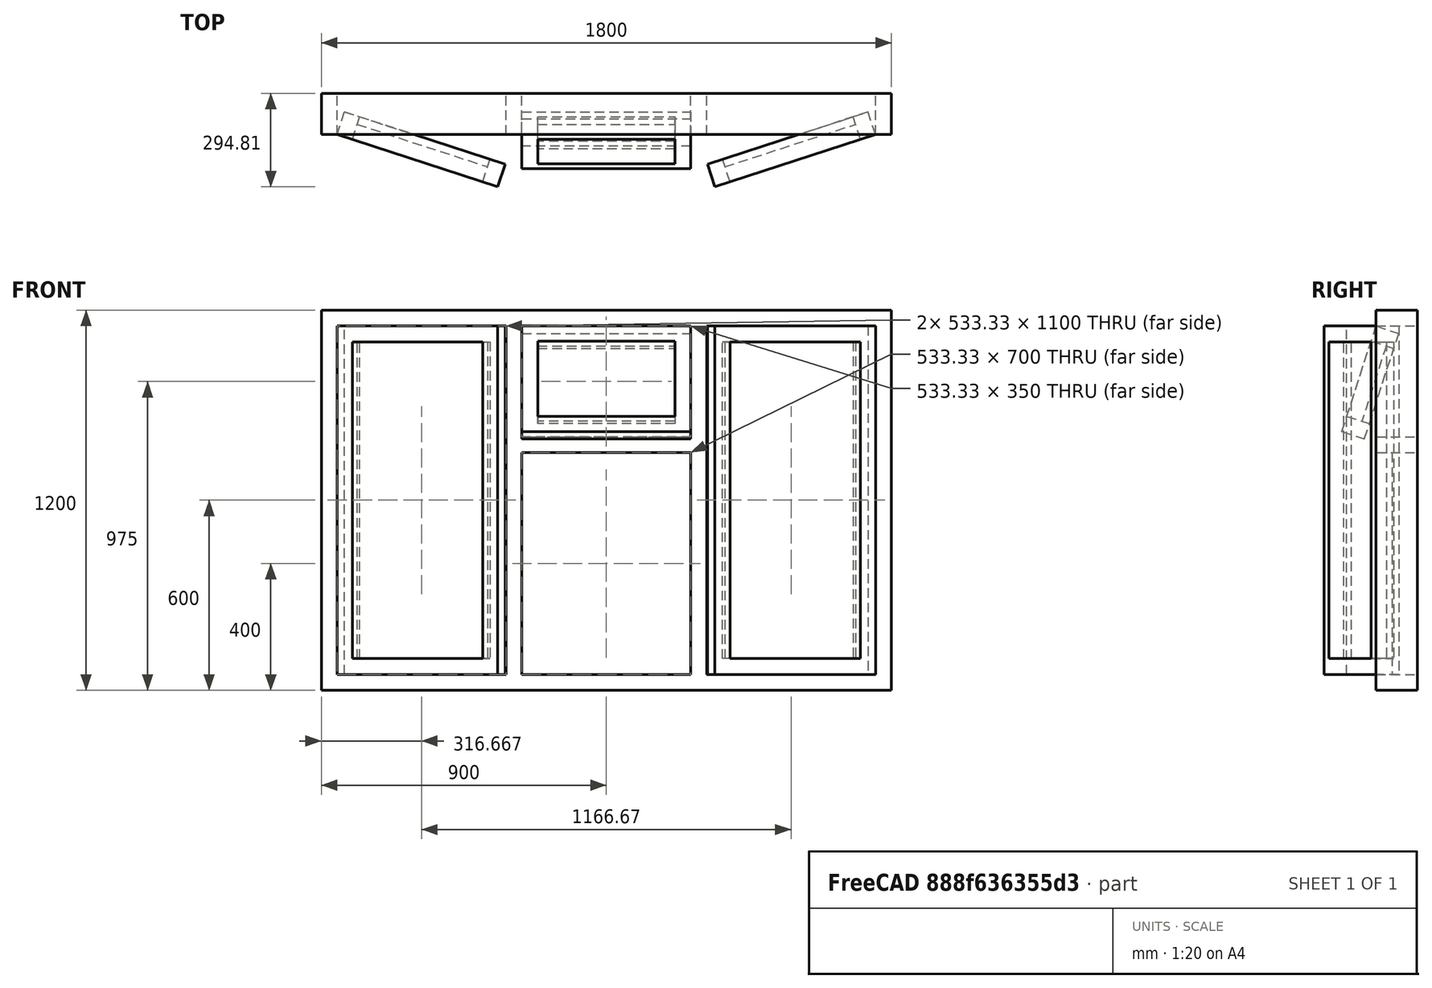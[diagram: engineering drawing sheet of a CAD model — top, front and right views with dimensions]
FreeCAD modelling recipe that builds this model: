
FCSTD DOCUMENT  (FreeCAD 0.19R23578 (Git))
Label: ThreeSectionTopSidesOpen
License: Creative Commons Attribution-ShareAlike
LicenseURL: http://creativecommons.org/licenses/by-sa/4.0/
objects: Sketcher::SketchObject×1, Part::FeaturePython×1
note: 2 computed .brp shape members not serialized (recipe doc carries the construction recipe); baked Part::Feature solids carry a one-line shape summary decoded from their .brp

FEATURE [Sketcher::SketchObject] Sketch
  Placement = pos=(0,0,0) rot=(1,0,0;1.5708rad)
  expr: .Constraints.OpeningFrame = .Constraints.Frame
  expr: .Constraints.CentreWidth = (.Constraints.Width - 4 * .Constraints.Frame) / 3
  sketch-geometry (53):
    g0: LineSegment StartX=0 StartY=1200 StartZ=0 EndX=1800 EndY=1200 EndZ=0
    g1: LineSegment StartX=1800 StartY=1200 StartZ=0 EndX=1800 EndY=0 EndZ=0
    g2: LineSegment StartX=1800 StartY=0 StartZ=0 EndX=0 EndY=0 EndZ=0
    g3: LineSegment StartX=0 StartY=0 StartZ=0 EndX=0 EndY=1200 EndZ=0
    g4: LineSegment StartX=50 StartY=1150 StartZ=0 EndX=583.333 EndY=1150 EndZ=0
    g5: LineSegment StartX=583.333 StartY=1150 StartZ=0 EndX=583.333 EndY=50 EndZ=0
    g6: LineSegment StartX=583.333 StartY=50 StartZ=0 EndX=50 EndY=50 EndZ=0
    g7: LineSegment StartX=50 StartY=50 StartZ=0 EndX=50 EndY=1150 EndZ=0
    g8: LineSegment StartX=633.333 StartY=1150 StartZ=0 EndX=1166.67 EndY=1150 EndZ=0
    g9: LineSegment StartX=1166.67 StartY=1150 StartZ=0 EndX=1166.67 EndY=800 EndZ=0
    g10: LineSegment StartX=1166.67 StartY=800 StartZ=0 EndX=633.333 EndY=800 EndZ=0
    g11: LineSegment StartX=633.333 StartY=800 StartZ=0 EndX=633.333 EndY=1150 EndZ=0
    g12: LineSegment StartX=683.333 StartY=1100 StartZ=0 EndX=1116.67 EndY=1100 EndZ=0
    g13: LineSegment StartX=1116.67 StartY=1100 StartZ=0 EndX=1116.67 EndY=850 EndZ=0
    g14: LineSegment StartX=1116.67 StartY=850 StartZ=0 EndX=683.333 EndY=850 EndZ=0
    g15: LineSegment StartX=683.333 StartY=850 StartZ=0 EndX=683.333 EndY=1100 EndZ=0
    g16: LineSegment StartX=1216.67 StartY=1150 StartZ=0 EndX=1750 EndY=1150 EndZ=0
    g17: LineSegment StartX=1750 StartY=1150 StartZ=0 EndX=1750 EndY=50 EndZ=0
    g18: LineSegment StartX=1750 StartY=50 StartZ=0 EndX=1216.67 EndY=50 EndZ=0
    g19: LineSegment StartX=1216.67 StartY=50 StartZ=0 EndX=1216.67 EndY=1150 EndZ=0
    g20: LineSegment StartX=633.333 StartY=750 StartZ=0 EndX=1166.67 EndY=750 EndZ=0
    g21: LineSegment StartX=1166.67 StartY=750 StartZ=0 EndX=1166.67 EndY=50 EndZ=0
    g22: LineSegment StartX=1166.67 StartY=50 StartZ=0 EndX=633.333 EndY=50 EndZ=0
    g23: LineSegment StartX=633.333 StartY=50 StartZ=0 EndX=633.333 EndY=750 EndZ=0
    g24: LineSegment StartX=100 StartY=1100 StartZ=0 EndX=533.333 EndY=1100 EndZ=0
    g25: LineSegment StartX=533.333 StartY=1100 StartZ=0 EndX=533.333 EndY=100 EndZ=0
    g26: LineSegment StartX=533.333 StartY=100 StartZ=0 EndX=100 EndY=100 EndZ=0
    g27: LineSegment StartX=100 StartY=100 StartZ=0 EndX=100 EndY=1100 EndZ=0
    g28: LineSegment StartX=1266.67 StartY=1100 StartZ=0 EndX=1700 EndY=1100 EndZ=0
    g29: LineSegment StartX=1700 StartY=1100 StartZ=0 EndX=1700 EndY=100 EndZ=0
    g30: LineSegment StartX=1700 StartY=100 StartZ=0 EndX=1266.67 EndY=100 EndZ=0
    g31: LineSegment StartX=1266.67 StartY=100 StartZ=0 EndX=1266.67 EndY=1100 EndZ=0
    g32: LineSegment StartX=1700 StartY=1100 StartZ=0 EndX=1750 EndY=1100 EndZ=0
    g33: LineSegment StartX=1700 StartY=1100 StartZ=0 EndX=1700 EndY=1150 EndZ=0
    g34: LineSegment StartX=1750 StartY=50 StartZ=0 EndX=1800 EndY=50 EndZ=0
    g35: LineSegment StartX=1266.67 StartY=100 StartZ=0 EndX=1266.67 EndY=50 EndZ=0
    g36: LineSegment StartX=1266.67 StartY=100 StartZ=0 EndX=1216.67 EndY=100 EndZ=0
    g37: LineSegment StartX=50 StartY=1150 StartZ=0 EndX=0 EndY=1150 EndZ=0
    g38: LineSegment StartX=100 StartY=1100 StartZ=0 EndX=50 EndY=1100 EndZ=0
    g39: LineSegment StartX=533.333 StartY=1100 StartZ=0 EndX=583.333 EndY=1100 EndZ=0
    g40: LineSegment StartX=683.333 StartY=1100 StartZ=0 EndX=633.333 EndY=1100 EndZ=0
    g41: LineSegment StartX=1116.67 StartY=1100 StartZ=0 EndX=1166.67 EndY=1100 EndZ=0
    g42: LineSegment StartX=683.333 StartY=850 StartZ=0 EndX=683.333 EndY=800 EndZ=0
    g43: LineSegment StartX=583.333 StartY=50 StartZ=0 EndX=583.333 EndY=0 EndZ=0
    g44: LineSegment StartX=583.333 StartY=0 StartZ=0 EndX=633.333 EndY=50 EndZ=0
    g45: LineSegment StartX=50 StartY=50 StartZ=0 EndX=0 EndY=50 EndZ=0
    g46: LineSegment StartX=0 StartY=0 StartZ=0 EndX=50 EndY=50 EndZ=0
    g47: LineSegment StartX=633.333 StartY=750 StartZ=0 EndX=583.333 EndY=750 EndZ=0
    g48: LineSegment StartX=583.333 StartY=750 StartZ=0 EndX=633.333 EndY=800 EndZ=0
    g49: LineSegment StartX=1216.67 StartY=50 StartZ=0 EndX=1216.67 EndY=0 EndZ=0
    g50: LineSegment StartX=1166.67 StartY=50 StartZ=0 EndX=1216.67 EndY=0 EndZ=0
    g51: LineSegment StartX=50 StartY=1150 StartZ=0 EndX=0 EndY=1200 EndZ=0
    g52: LineSegment StartX=1750 StartY=50 StartZ=0 EndX=1800 EndY=0 EndZ=0
  constraints (152):
    c: Coincident(g0,g1)
    c: Coincident(g1,g2)
    c: Coincident(g2,g3)
    c: Coincident(g3,g0)
    c: Horizontal(g0)
    c: Horizontal(g2)
    c: Vertical(g1)
    c: Vertical(g3)
    c: Coincident(g4,g5)
    c: Coincident(g5,g6)
    c: Coincident(g6,g7)
    c: Coincident(g7,g4)
    c: Horizontal(g4)
    c: Horizontal(g6)
    c: Vertical(g5)
    c: Vertical(g7)
    c: Coincident(g8,g9)
    c: Coincident(g9,g10)
    c: Coincident(g11,g8)
    c: Horizontal(g8)
    c: Horizontal(g10)
    c: Vertical(g9)
    c: Vertical(g11)
    c: Coincident(g12,g13)
    c: Coincident(g13,g14)
    c: Coincident(g14,g15)
    c: Coincident(g15,g12)
    c: Horizontal(g12)
    c: Horizontal(g14)
    c: Vertical(g13)
    c: Coincident(g16,g17)
    c: Coincident(g17,g18)
    c: Coincident(g18,g19)
    c: Coincident(g19,g16)
    c: Horizontal(g16)
    c: Horizontal(g18)
    c: Vertical(g17)
    c: Vertical(g19)
    c: Coincident(g20,g21)
    c: Coincident(g21,g22)
    c: Coincident(g22,g23)
    c: Horizontal(g20)
    c: Horizontal(g22)
    c: Vertical(g21)
    c: Vertical(g23)
    c: Coincident(g24,g25)
    c: Coincident(g25,g26)
    c: Coincident(g26,g27)
    c: Coincident(g27,g24)
    c: Horizontal(g24)
    c: Horizontal(g26)
    c: Vertical(g25)
    c: Vertical(g27)
    c: Coincident(g28,g29)
    c: Coincident(g29,g30)
    c: Coincident(g30,g31)
    c: Coincident(g31,g28)
    c: Horizontal(g28)
    c: Horizontal(g30)
    c: Vertical(g29)
    c: Vertical(g31)
    c: Horizontal(g5,g22)
    c: Horizontal(g21,g18)
    c: Horizontal(g4,g8)
    c: Horizontal(g12,g24)
    c: Horizontal(g25,g30)
    c: Horizontal(g28,g12)
    c: Horizontal(g8,g16)
    c: Vertical(g20,g9)
    c: Distance(g6,g3) = 50  'Frame'
    c: Distance(g26,g7) = 50  'OpeningFrame'
    c: DistanceY(g3,g3) = 1200  'Height'
    c: DistanceX(g0,g0) = 1800  'Width'
    c: Coincident(g32,g28)
    c: Horizontal(g32,g28)
    c: Coincident(g33,g28)
    c: PointOnObject(g33,g16)
    c: Vertical(g33)
    c: Coincident(g34,g17)
    c: PointOnObject(g34,g1)
    c: Horizontal(g34)
    c: Coincident(g35,g30)
    c: PointOnObject(g35,g18)
    c: Vertical(g35)
    c: Coincident(g36,g30)
    c: PointOnObject(g36,g19)
    c: Horizontal(g36)
    c: Coincident(g37,g4)
    c: PointOnObject(g37,g3)
    c: Horizontal(g37)
    c: Coincident(g38,g24)
    c: Horizontal(g38)
    c: Coincident(g39,g24)
    c: PointOnObject(g39,g5)
    c: Horizontal(g39)
    c: Coincident(g40,g12)
    c: PointOnObject(g40,g11)
    c: Coincident(g41,g12)
    c: PointOnObject(g41,g9)
    c: Horizontal(g41)
    c: Coincident(g42,g14)
    c: PointOnObject(g42,g10)
    c: Vertical(g42)
    c: Horizontal(g40)
    c: Equal(g38,g39)
    c: Equal(g39,g40)
    c: Equal(g40,g42)
    c: Equal(g42,g41)
    c: Equal(g41,g33)
    c: Equal(g33,g32)
    c: Equal(g32,g35)
    c: Equal(g35,g36)
    c: PointOnObject(g38,g7)
    c: Equal(g15,g13)
    c: PointOnObject(g32,g17)
    c: Coincident(g20,g23)
    c: Coincident(g11,g10)
    c: Distance(g9) = 350  'TopOpenHeight'
    c: Equal(g18,g6)
    c: Distance(g22) = 533.333  'CentreWidth'
    c: Coincident(g43,g5)
    c: PointOnObject(g43,g2)
    c: Vertical(g43)
    c: Coincident(g44,g43)
    c: Coincident(g44,g22)
    c: Angle(g44,g43) = 0.785398
    c: Coincident(g45,g6)
    c: PointOnObject(g45,g3)
    c: Horizontal(g45)
    c: Coincident(g46,g2)
    c: Coincident(g46,g6)
    c: Angle(g45,g46) = 0.785398
    c: Coincident(g47,g20)
    c: PointOnObject(g47,g5)
    c: Horizontal(g47)
    c: Coincident(g48,g47)
    c: Coincident(g48,g10)
    c: Angle(g47,g48) = 0.785398
    c: Coincident(g49,g18)
    c: PointOnObject(g49,g2)
    c: Vertical(g49)
    c: Coincident(g50,g21)
    c: Coincident(g50,g49)
    c: Angle(g49,g50) = 0.785398
    c: Vertical(g10,g20)
    c: Coincident(g51,g4)
    c: Coincident(g51,g0)
    c: Angle(g51,g37) = 0.785398
    c: Coincident(g52,g17)
    c: Coincident(g52,g1)
    c: Equal(g34,g45)
    c: Coincident(g-1,g2)
FEATURE [Part::FeaturePython] Window  # Arch/BIM 170 (typed FeaturePython)
  Area = 0
  Base = -> Sketch
  Frame = 50
  Height = 0
  HoleDepth = 0
  HoleWire = 1
  HorizontalArea = 0
  IfcData = attributes={"GlobalId": {"name": "GlobalId", "type": "IfcGloballyUniqueId", "is_enum": false, "enum_values": []}, "Description": {"... (+1228 chars omitted),+1 more (map truncated)
  IfcType = 170
  LouvreSpacing = 0
  LouvreWidth = 0
  MoveBase = true
  MoveWithHost = true
  Normal = (0,1,0)
  Opening = 40
  OverallHeight = 0
  OverallWidth = 1800
  PartitioningType = 0
  PerimeterLength = 0
  PredefinedType = 0
  Preset = 0
  SymbolElevation = false
  SymbolPlan = false
  VerticalArea = 0
  Width = 1800
  WindowParts = OutFrame | Frame | Wire0,Wire1,Wire2,Wire4,Wire5 | 130.0 | 0.0 | FixedGlass | Glass panel | Wire5 | 50.0 | 0.0 | TopFrame | Frame | Wire2,Wire3,Edge9,Mode4 | 75.0 | 0.0 | TopGlass | Glass panel | Wire3 | 50.0 | 0.0 | RightFrame | Frame | Wire4,Wire7,Edge18,Mode3 | 75.0 | 0.0 | RightGlass | Glass panel | Wire7 | 50.0 | 0.0 | LeftFrame | Frame | Wire1,Wire6,Edge8,Mode4 | 75.0 | 0.0 | LeftGlass | Glass panel | Wire6 | 50.0 | 0.0
  expr: OverallWidth = .Width.Value
  expr: OverallHeight = .Height.Value
